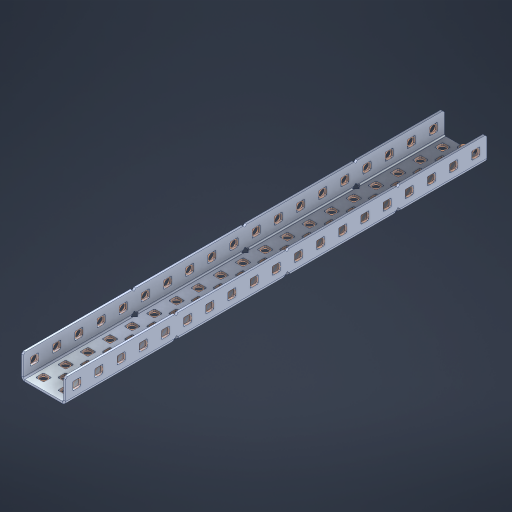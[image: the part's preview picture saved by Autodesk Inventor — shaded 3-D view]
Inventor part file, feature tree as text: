
AUTODESK INVENTOR PART (.ipt)
format: ipt  version: 2023 (Build 270158000, 158)  size: 1,341,952 bytes
history: native  units: in
note: dims shown in document units (in); Inventor stores cm internally (conversion verified against a paired STEP export)
features: other x102, extrude x93, sheet_metal_op x11, sketch x10, pattern_linear x2, mirror x1, chamfer x1
ambient origin geometry x8: Origin, YZ Plane, XZ Plane, XY Plane, X Axis, Y Axis, Z Axis, Center Point
bodies: Solid1 (feature_tree), Body (feature_tree)
feature tree (220):
  sheet_metal_op  "Flanges"
  other  "Flange Pattern Plane"
  other  "Flange Pattern Sketch"
  sheet_metal_op  "Flange Pattern"
  sheet_metal_op  "Body Pattern"
  pattern_linear  "Center Pattern"  Spacing1=0.0469in  [1 undecoded]
  other  "Arc Length"
  mirror  "Notch Mirror"
  pattern_linear  "Notch Pattern"  Spacing1=0.182in  [1 undecoded]
  chamfer  "End Chamfer"
  extrude  "Half Cut"  Depth=0.02in
  sketch  "Sketch1"  dims[d0=1.0in]
  other  "Plate1"
  sketch  "Sketch2"  dims[d1=9.5in]
  other  "Plate2"
  sheet_metal_op  "Bend1"
  sheet_metal_op  "Corner1"
  sketch  "Sketch3"  dims[d2=0.0469in]
  sketch  "Sketch7"  dims[d3=0.0469in]
  other  "Srf1"
  other  "Srf2"
  sketch  "Sketch8"  dims[d4=0.0234in]
  sketch  "Sketch9"  dims[d5=0.0938in]
  other  "Srf91"
  sheet_metal_op  "Body Pattern Sketch"
  other  "Srf92"
  sketch  "Sketch13"  dims[d6=0.0469in]
  sketch  "Sketch14"  dims[d7=0.5in d8=90.0deg d9=0.0312in]
  sketch  "Sketch15"  dims[d10=0.1875in]
  sketch  "Sketch16"  dims[d11=0.0469in d12=0.0469in d16=0.182in d17=0.02in d18=0.0469in d19=0.0in d20=0.25in d21=0.25in d38=7.4803in d40=0.5in d41=0.7874in d43=1.0in d46=0.172in d47=1.0in d48=0.0in d49=0.182in d50=0.02in d51=0.25in d52=0.25in d53=0.0469in d54=0.0in d55=0.172in d56=1.0in d57=0.0in d58=0.25in d60=7.4803in d62=0.5in d63=0.7874in d65=0.5in d85=0.1227in d86=0.1659in d88=0.04in d89=0.0469in d90=0.0in d91=0.04in d92=0.0491in d95=2.5in d96=0.04in d97=0.25in d98=45.0deg d99=0.25in d100=0.5in d101=0.0in d102=2.497in d106=0.182in d107=0.02in d108=0.5in d109=0.5in d110=0.0469in d111=0.0in d112=0.172in d113=0.5in d114=0.0in d117=0.5in d118=0.5in d119=0.5in]
  other  "Srf786"
  other  "Srf823"
  other  "Srf824"
  other  "Srf825"
  other  "Srf826"
  other  "Srf827"
  other  "Srf828"
  other  "Srf829"
  other  "Srf856"
  other  "Srf857"
  other  "Srf858"
  other  "Srf859"
  other  "Srf860"
  other  "Srf861"
  other  "Srf862"
  other  "Srf889"
  other  "Srf890"
  other  "Srf891"
  other  "Srf892"
  other  "Srf893"
  other  "Srf894"
  other  "Srf895"
  other  "Srf896"
  other  "Srf922"
  other  "Srf923"
  other  "Srf924"
  other  "Srf925"
  other  "Srf926"
  other  "Srf959"
  other  "Srf960"
  other  "Srf961"
  other  "Srf962"
  other  "Srf963"
  other  "Srf996"
  other  "Srf997"
  other  "Srf998"
  other  "Srf999"
  other  "Srf1000"
  other  "Srf1143"
  other  "Srf1144"
  other  "Srf1145"
  other  "Srf1146"
  other  "Srf1147"
  other  "Srf1148"
  other  "Srf1149"
  other  "Srf1150"
  other  "Srf1151"
  other  "Srf1152"
  other  "Srf1153"
  other  "Srf1154"
  other  "Srf1155"
  other  "Srf1156"
  other  "Srf1157"
  other  "Srf1158"
  other  "Srf1159"
  other  "Srf1160"
  other  "Srf1161"
  other  "Srf1162"
  other  "Srf1163"
  other  "Srf1164"
  other  "Srf1165"
  other  "Srf1166"
  other  "Srf1199"
  other  "Srf1200"
  other  "Srf1201"
  other  "Srf1202"
  other  "Srf1203"
  other  "Srf1204"
  other  "Srf1205"
  other  "Srf1206"
  other  "Srf1207"
  other  "Srf1208"
  other  "Srf1209"
  other  "Srf1210"
  other  "Srf1211"
  other  "Srf1212"
  other  "Srf1213"
  other  "Srf1214"
  other  "Srf1215"
  other  "Srf1216"
  other  "Srf1217"
  other  "Srf1218"
  other  "Srf1219"
  other  "Srf1220"
  other  "Srf1221"
  other  "Srf1222"
  other  "Srf1255"
  other  "Srf1256"
  other  "Srf1257"
  other  "Srf1258"
  other  "Srf1259"
  sheet_metal_op  "Flange Stamp"
  sheet_metal_op  "Flange Circle"
  sheet_metal_op  "Body Stamp"
  sheet_metal_op  "Body Circle"
  other  "Center Stamp"
  other  "Center Circle"
  sheet_metal_op  "Notch"
  extrude  "ExtrusionSrf2"  Depth=0.0469in
  extrude  "ExtrusionSrf92"  TaperAngle=0.0deg  [1 undecoded]
  extrude  "ExtrusionSrf823"  Depth=0.5in
  extrude  "ExtrusionSrf824"  Depth=0.5in
  extrude  "ExtrusionSrf825"  Depth=0.5in
  extrude  "ExtrusionSrf826"  Depth=0.5in
  extrude  "ExtrusionSrf827"  Depth=1.0in TaperAngle=0.0deg
  extrude  "ExtrusionSrf828"  Depth=0.5in
  extrude  "ExtrusionSrf829"  Depth=0.02in
  extrude  "ExtrusionSrf856"  Depth=0.5in
  extrude  "ExtrusionSrf857"  Depth=0.5in
  extrude  "ExtrusionSrf858"  Depth=0.0469in
  extrude  "ExtrusionSrf859"  TaperAngle=0.0deg  [1 undecoded]
  extrude  "ExtrusionSrf860"  Depth=0.5in
  extrude  "ExtrusionSrf861"  Depth=1.0in TaperAngle=0.0deg
  extrude  "ExtrusionSrf862"  Depth=0.5in
  extrude  "ExtrusionSrf889"  Depth=0.5in
  extrude  "ExtrusionSrf890"  Depth=0.5in
  extrude  "ExtrusionSrf891"  Depth=0.5in
  extrude  "ExtrusionSrf892"  Depth=0.5in
  extrude  "ExtrusionSrf893"  Depth=0.5in
  extrude  "ExtrusionSrf894"  Depth=0.0469in
  extrude  "ExtrusionSrf895"  TaperAngle=0.0deg  [1 undecoded]
  extrude  "ExtrusionSrf896"  Depth=0.5in
  extrude  "ExtrusionSrf922"  Depth=0.5in
  extrude  "ExtrusionSrf923"  Depth=2.5in
  extrude  "ExtrusionSrf924"  Depth=0.5in TaperAngle=45.0deg
  extrude  "ExtrusionSrf925"  Depth=0.5in
  extrude  "ExtrusionSrf926"  Depth=0.5in TaperAngle=0.0deg
  extrude  "ExtrusionSrf959"  Depth=0.5in
  extrude  "ExtrusionSrf960"  Depth=0.5in
  extrude  "ExtrusionSrf961"  Depth=0.02in
  extrude  "ExtrusionSrf962"  Depth=0.5in
  extrude  "ExtrusionSrf963"  Depth=0.5in
  extrude  "ExtrusionSrf996"  Depth=0.0469in
  extrude  "ExtrusionSrf997"  TaperAngle=0.0deg  [1 undecoded]
  extrude  "ExtrusionSrf998"  Depth=0.5in
  extrude  "ExtrusionSrf999"  Depth=0.5in TaperAngle=0.0deg
  extrude  "ExtrusionSrf1000"  Depth=0.5in
  extrude  "ExtrusionSrf1143"  Depth=0.5in
  extrude  "ExtrusionSrf1144"  Depth=0.5in
  extrude  "ExtrusionSrf1145"  [1 undecoded]
  extrude  "ExtrusionSrf1146"  [1 undecoded]
  extrude  "ExtrusionSrf1147"  [1 undecoded]
  extrude  "ExtrusionSrf1148"  [1 undecoded]
  extrude  "ExtrusionSrf1149"  [1 undecoded]
  extrude  "ExtrusionSrf1150"  [1 undecoded]
  extrude  "ExtrusionSrf1151"  [1 undecoded]
  extrude  "ExtrusionSrf1152"  [1 undecoded]
  extrude  "ExtrusionSrf1153"  [1 undecoded]
  extrude  "ExtrusionSrf1154"  [1 undecoded]
  extrude  "ExtrusionSrf1155"  [1 undecoded]
  extrude  "ExtrusionSrf1156"  [1 undecoded]
  extrude  "ExtrusionSrf1157"  [1 undecoded]
  extrude  "ExtrusionSrf1158"  [1 undecoded]
  extrude  "ExtrusionSrf1159"  [1 undecoded]
  extrude  "ExtrusionSrf1160"  [1 undecoded]
  extrude  "ExtrusionSrf1161"  [1 undecoded]
  extrude  "ExtrusionSrf1162"  [1 undecoded]
  extrude  "ExtrusionSrf1163"  [1 undecoded]
  extrude  "ExtrusionSrf1164"  [1 undecoded]
  extrude  "ExtrusionSrf1165"  [1 undecoded]
  extrude  "ExtrusionSrf1166"  [1 undecoded]
  extrude  "ExtrusionSrf1199"  [1 undecoded]
  extrude  "ExtrusionSrf1200"  [1 undecoded]
  extrude  "ExtrusionSrf1201"  [1 undecoded]
  extrude  "ExtrusionSrf1202"  [1 undecoded]
  extrude  "ExtrusionSrf1203"  [1 undecoded]
  extrude  "ExtrusionSrf1204"  [1 undecoded]
  extrude  "ExtrusionSrf1205"  [1 undecoded]
  extrude  "ExtrusionSrf1206"  [1 undecoded]
  extrude  "ExtrusionSrf1207"  [1 undecoded]
  extrude  "ExtrusionSrf1208"  [1 undecoded]
  extrude  "ExtrusionSrf1209"  [1 undecoded]
  extrude  "ExtrusionSrf1210"  [1 undecoded]
  extrude  "ExtrusionSrf1211"  [1 undecoded]
  extrude  "ExtrusionSrf1212"  [1 undecoded]
  extrude  "ExtrusionSrf1213"  [1 undecoded]
  extrude  "ExtrusionSrf1214"  [1 undecoded]
  extrude  "ExtrusionSrf1215"  [1 undecoded]
  extrude  "ExtrusionSrf1216"  [1 undecoded]
  extrude  "ExtrusionSrf1217"  [1 undecoded]
  extrude  "ExtrusionSrf1218"  [1 undecoded]
  extrude  "ExtrusionSrf1219"  [1 undecoded]
  extrude  "ExtrusionSrf1220"  [1 undecoded]
  extrude  "ExtrusionSrf1221"  [1 undecoded]
  extrude  "ExtrusionSrf1222"  [1 undecoded]
  extrude  "ExtrusionSrf1255"  [1 undecoded]
  extrude  "ExtrusionSrf1256"  [1 undecoded]
  extrude  "ExtrusionSrf1257"  [1 undecoded]
  extrude  "ExtrusionSrf1258"  [1 undecoded]
  extrude  "ExtrusionSrf1259"  [1 undecoded]
note: 57 required parameter values undecoded (feature->parameter linkage not recoverable at this tier; creation-order binding heuristic only, values carry confidence <= 0.55)
